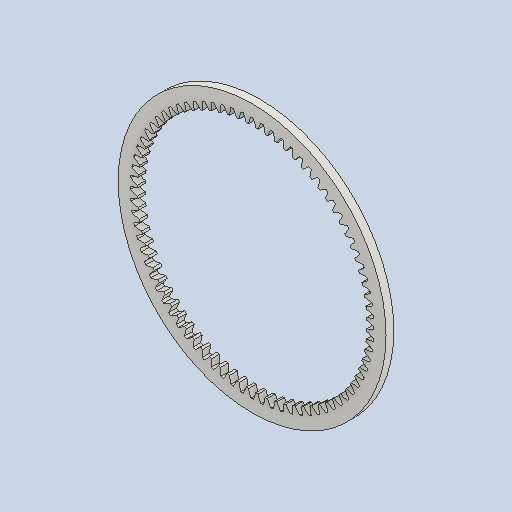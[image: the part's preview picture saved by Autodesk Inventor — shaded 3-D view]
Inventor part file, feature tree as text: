
AUTODESK INVENTOR PART (.ipt)
format: ipt  version: 2024 (Build 280153000, 153)  size: 416,768 bytes
history: native  units: mm (DEFAULTED — no unit token found)
features: plane x3, other x3, extrude x1, sketch x1
ambient origin geometry x8: Origin, YZ Plane, XZ Plane, XY Plane, X Axis, Y Axis, Z Axis, Center Point
bodies: Solid1 (feature_tree)
feature tree (8):
  extrude  "Extrusion1"  Depth=5.0mm TaperAngle=0.0deg
  plane  "Work Plane2"
  plane  "Work Plane8"
  plane  "Work Plane9"
  other  "Spur Gear"
  sketch  "Sketch1"  dims[d0=172.7mm d1=5.0mm d2=0.0mm d3=152.0mm d4=10.0mm d5=0.0mm d16=57.0mm d17=0.0mm d34=0.413367mm d39=0.0mm d45=0.0mm d47=57.0mm d50=0.0mm d51=0.0mm d52=57.0mm]
  other  "Srf1"
  other  "Pitch Diameter"
